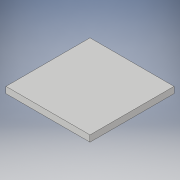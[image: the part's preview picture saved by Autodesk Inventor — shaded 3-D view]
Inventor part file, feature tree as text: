
AUTODESK INVENTOR PART (.ipt)
format: ipt  version: 2019 (Build 230136000, 136)  size: 90,112 bytes
history: native  units: mm
features: extrude x1, sketch x1
ambient origin geometry x8: Origin, YZ Plane, XZ Plane, XY Plane, X Axis, Y Axis, Z Axis, Center Point
bodies: Solid1 (feature_tree)
feature tree (2):
  extrude  "Extrusion1"  Depth=400.0mm
  sketch  "Sketch1"  dims[d0=400.0mm d1=400.0mm d2=400.0mm d3=30.0mm d4=0.0mm]
